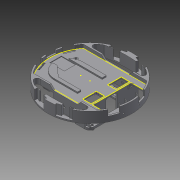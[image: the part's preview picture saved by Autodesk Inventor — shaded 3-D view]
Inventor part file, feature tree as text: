
AUTODESK INVENTOR PART (.ipt)
format: ipt  version: 2014 (Build 180170000, 170)  size: 1,046,528 bytes
history: native  units: mm
features: reference x63, sketch x40, extrude x37, plane x17, other x6, fillet x5, mirror x4, chamfer x4, hole x3, projected_geometry x2
ambient origin geometry x8: Origin, YZ Plane, XZ Plane, XY Plane, X Axis, Y Axis, Z Axis, Center Point
bodies: Volumenkörper1 (feature_tree)
feature tree (181):
  sketch  "Skizze1"  dims[d0=2.0mm d1=2.0mm]
  other  "Arbeitsachse1"
  other  "Arbeitsachse2"
  plane  "Arbeitsebene1"
  extrude  "Extrusion1"  Depth=2.0mm
  sketch  "Skizze2"  dims[d2=10.0mm d3=0.0mm d4=2.0mm]
  plane  "Arbeitsebene2"
  extrude  "Extrusion2"  Depth=2.0mm
  sketch  "Skizze3"  dims[d5=5.0mm d6=10.0mm d7=0.0mm]
  plane  "Arbeitsebene3"
  extrude  "Extrusion3"  Depth=10.0mm TaperAngle=0.0deg
  extrude  "Extrusion4"  Depth=10.0mm TaperAngle=0.0deg
  plane  "Arbeitsebene13"
  extrude  "Extrusion5"  Depth=0.5mm TaperAngle=0.0deg
  mirror  "Spiegeln1"
  extrude  "Extrusion6"  Depth=2.0mm
  extrude  "Extrusion7"  Depth=2.0mm TaperAngle=0.0deg
  extrude  "Extrusion8"  Depth=10.0mm
  fillet  "Rundung1"  Radius=1.5mm
  sketch  "Skizze25"  dims[d169=30.0deg d170=3.490659mm]
  plane  "Arbeitsebene12"
  extrude  "Extrusion25"  Depth=3.490659mm
  extrude  "Extrusion26"  TaperAngle=0.0deg  [1 undecoded]
  extrude  "Extrusion27"  Depth=2.0mm
  mirror  "Spiegeln3"
  extrude  "Extrusion9"  Depth=2.0mm TaperAngle=0.0deg
  extrude  "Extrusion28"  Depth=2.0mm
  extrude  "Extrusion29"  Depth=2.0mm TaperAngle=45.0deg
  extrude  "Extrusion30"  Depth=8.0mm
  chamfer  "Fase1"  Distance=2.0mm
  mirror  "Spiegeln4"
  sketch  "Skizze31"  dims[d187=8.0mm d188=8.0mm]
  other  "Arbeitsachse6"
  extrude  "Extrusion31"  Depth=3.0mm
  extrude  "Extrusion38"  Depth=3.0mm TaperAngle=0.0deg
  extrude  "Extrusion32"  Depth=3.0mm TaperAngle=0.0deg
  extrude  "Extrusion33"  Depth=10.0mm TaperAngle=0.0deg
  extrude  "Extrusion47"  Depth=10.0mm
  plane  "Arbeitsebene16"
  extrude  "Extrusion34"  TaperAngle=45.0deg  [1 undecoded]
  plane  "Arbeitsebene18"
  extrude  "Extrusion35"  Depth=3.0mm
  plane  "Arbeitsebene20"
  extrude  "Extrusion36"  Depth=3.0mm
  plane  "Arbeitsebene22"
  extrude  "Extrusion37"  Depth=2.0mm
  plane  "Arbeitsebene24"
  extrude  "Extrusion39"  Depth=3.0mm
  extrude  "Extrusion40"  Depth=15.0mm
  plane  "Arbeitsebene26"
  hole  "Bohrung1"  [1 undecoded]
  other  "Rippe1"
  fillet  "Rundung2"  Radius=7.0mm
  extrude  "Extrusion46"  Depth=3.0mm
  chamfer  "Fase2"  Distance=13.0mm
  extrude  "Extrusion41"  Depth=5.0mm
  extrude  "Extrusion42"  Depth=0.5mm
  extrude  "Extrusion44"  Depth=4.0mm
  mirror  "Spiegeln5"
  fillet  "Rundung3"  Radius=30.0mm
  extrude  "Extrusion45"  Depth=4.0mm
  fillet  "Rundung4"  Radius=4.0mm
  plane  "Arbeitsebene28"
  extrude  "Extrusion48"  Depth=1.5mm
  hole  "Bohrung2"  [1 undecoded]
  sketch  "Skizze54"  dims[d254=0.5mm d255=0.5mm]
  other  "Arbeitspunkt3"
  extrude  "Extrusion49"  Depth=2.0mm
  chamfer  "Fase3"  Distance=2.0mm
  chamfer  "Fase4"  Distance=2.0mm Angle=45.0deg
  extrude  "Extrusion53"  Depth=2.0mm TaperAngle=0.0deg
  hole  "Bohrung3"  [1 undecoded]
  fillet  "Rundung6"  Radius=4.0mm
  extrude  "Extrusion54"  Depth=2.0mm TaperAngle=0.0deg
  extrude  "Extrusion55"  Depth=24.0mm TaperAngle=0.0deg
  extrude  "Extrusion56"  Depth=24.0mm TaperAngle=45.0deg
  reference  "Referenz1"
  reference  "Referenz2"
  reference  "Referenz3"
  reference  "Referenz4"
  reference  "Referenz5"
  reference  "Referenz6"
  reference  "Referenz7"
  reference  "Referenz8"
  reference  "Referenz9"
  reference  "Referenz10"
  reference  "Referenz11"
  reference  "Referenz12"
  reference  "Referenz13"
  reference  "Referenz14"
  reference  "Referenz15"
  reference  "Referenz16"
  reference  "Referenz17"
  reference  "Referenz18"
  reference  "Referenz19"
  sketch  "Skizze4"  dims[d8=10.0mm d9=0.0mm d10=0.5mm d11=0.0mm]
  reference  "Referenz20"
  reference  "Referenz21"
  sketch  "Skizze5"  dims[d12=0.5mm d13=0.0mm d14=0.5mm d15=0.0mm]
  reference  "Referenz22"
  reference  "Referenz23"
  sketch  "Skizze6"  dims[d16=2.0mm d17=0.0mm d18=17.0mm]
  reference  "Referenz24"
  reference  "Referenz25"
  reference  "Referenz26"
  sketch  "Skizze7"  dims[d19=2.0mm d20=0.0mm d26=5.0mm d27=0.0mm]
  sketch  "Skizze8"  dims[d164=10.0mm d165=0.0mm d166=1.5mm d167=1.5mm d168=0.0mm]
  reference  "Referenz27"
  reference  "Referenz28"
  reference  "Referenz29"
  reference  "Referenz30"
  reference  "Referenz33"
  reference  "Referenz34"
  reference  "Referenz35"
  sketch  "Skizze26"  dims[d171=2.0mm d172=0.0mm d173=0.0mm]
  sketch  "Skizze27"  dims[d174=2.0mm d175=2.0mm]
  sketch  "Skizze28"  dims[d176=2.0mm d177=2.0mm d178=0.0mm]
  sketch  "Skizze29"  dims[d179=10.0mm d180=0.0mm d181=2.0mm]
  sketch  "Skizze30"  dims[d182=1.5mm d183=0.0mm d184=2.0mm d185=1.5mm d186=45.0deg]
  other  "Arbeitsachse5"
  sketch  "Skizze32"  dims[d189=5.0mm d190=2.0mm d191=0.0mm]
  sketch  "Skizze34"  dims[d196=3.0mm d197=0.0mm d198=2.9mm]
  plane  "Arbeitsebene15"
  sketch  "Skizze35"  dims[d199=3.0mm d200=0.0mm d202=3.0mm d203=0.0mm]
  reference  "Referenz47"
  reference  "Referenz48"
  reference  "Referenz49"
  reference  "Referenz50"
  plane  "Arbeitsebene17"
  sketch  "Skizze36"  dims[d204=3.0mm d205=0.0mm d206=5.5mm d207=0.0mm]
  reference  "Referenz51"
  reference  "Referenz52"
  reference  "Referenz53"
  reference  "Referenz54"
  plane  "Arbeitsebene19"
  sketch  "Skizze37"  dims[d208=5.5mm d209=0.0mm d210=10.0mm d211=0.0mm]
  plane  "Arbeitsebene21"
  sketch  "Skizze38"  dims[d212=10.0mm d213=0.0mm d214=6.0mm]
  sketch  "Skizze39"  dims[d215=3.0mm d216=0.0mm d218=45.0deg]
  reference  "Referenz63"
  reference  "Referenz64"
  reference  "Referenz65"
  reference  "Referenz66"
  reference  "Referenz67"
  reference  "Referenz68"
  reference  "Referenz69"
  reference  "Referenz70"
  reference  "Referenz71"
  plane  "Arbeitsebene23"
  sketch  "Skizze40"  dims[d219=3.0mm d220=7.0mm]
  reference  "Referenz72"
  sketch  "Skizze41"  dims[d221=7.0mm d222=3.0mm]
  projected_geometry  "Projizierte Kontur3"
  sketch  "Skizze43"  dims[d223=3.0mm d224=6.0mm d225=4.0mm d226=2.0mm d227=90.0deg d228=8.0mm d229=20.594885mm d230=15.0mm]
  sketch  "Skizze44"  dims[d231=3.0mm d232=9.0mm]
  sketch  "Skizze45"  dims[d233=9.0mm d234=15.0mm]
  sketch  "Skizze46"  dims[d235=3.0mm]
  reference  "Referenz73"
  reference  "Referenz74"
  reference  "Referenz75"
  reference  "Referenz76"
  reference  "Referenz77"
  reference  "Referenz78"
  reference  "Referenz79"
  reference  "Referenz80"
  sketch  "Skizze48"  dims[d236=1.0mm d237=0.5mm d238=0.0mm d239=0.0mm d240=1.0mm d241=1.0mm d242=6.0mm d243=7.0mm]
  sketch  "Skizze49"  dims[d244=3.0mm d245=0.0mm d246=0.5mm]
  sketch  "Skizze50"  dims[d247=0.5mm]
  projected_geometry  "Projizierte Kontur4"
  sketch  "Skizze51"  dims[d248=6.0mm]
  sketch  "Skizze52"  dims[d249=5.0mm d250=13.0mm d251=0.0mm]
  reference  "Referenz83"
  reference  "Referenz84"
  reference  "Referenz85"
  sketch  "Skizze53"  dims[d252=6.0mm d253=5.0mm]
  reference  "Referenz86"
  sketch  "Skizze58"  dims[d256=4.0mm d259=4.0mm d260=30.0mm]
  sketch  "Skizze59"  dims[d261=4.0mm d262=0.0mm d263=4.0mm d264=4.0mm]
  sketch  "Skizze60"  dims[d265=1.5mm d266=1.5mm]
  sketch  "Skizze61"  dims[d267=2.0mm d268=0.0mm d269=1.0mm]
  sketch  "Skizze62"  dims[d270=30.0mm d271=25.0mm d272=2.0mm d273=0.0mm d274=5.0mm d275=2.0mm d276=45.0deg d277=2.0mm d278=0.0mm d279=4.0mm d280=4.0mm d281=2.0mm d282=0.0mm d283=1.5mm d284=6.0mm d285=4.0mm d286=2.0mm d287=90.0deg d288=8.0mm d289=20.594885mm d290=24.0mm d291=0.0mm d294=5.0mm d295=24.0mm d296=45.0deg d297=5.0mm d298=24.0mm d299=45.0deg d310=2.0mm d311=2.0mm d312=2.0mm d313=2.0mm d314=12.0mm d315=0.0mm d316=21.0mm d317=9.0mm d318=4.0mm d319=3.7mm d320=2.8mm d321=6.0mm d322=4.0mm d323=2.0mm d324=90.0deg d325=8.0mm d326=20.594885mm d327=3.0mm d328=12.0mm d329=0.0mm d330=12.0mm d331=0.0mm d332=4.9mm d333=2.0mm d334=0.0mm]
note: 5 required parameter values undecoded (feature->parameter linkage not recoverable at this tier; creation-order binding heuristic only, values carry confidence <= 0.55)
